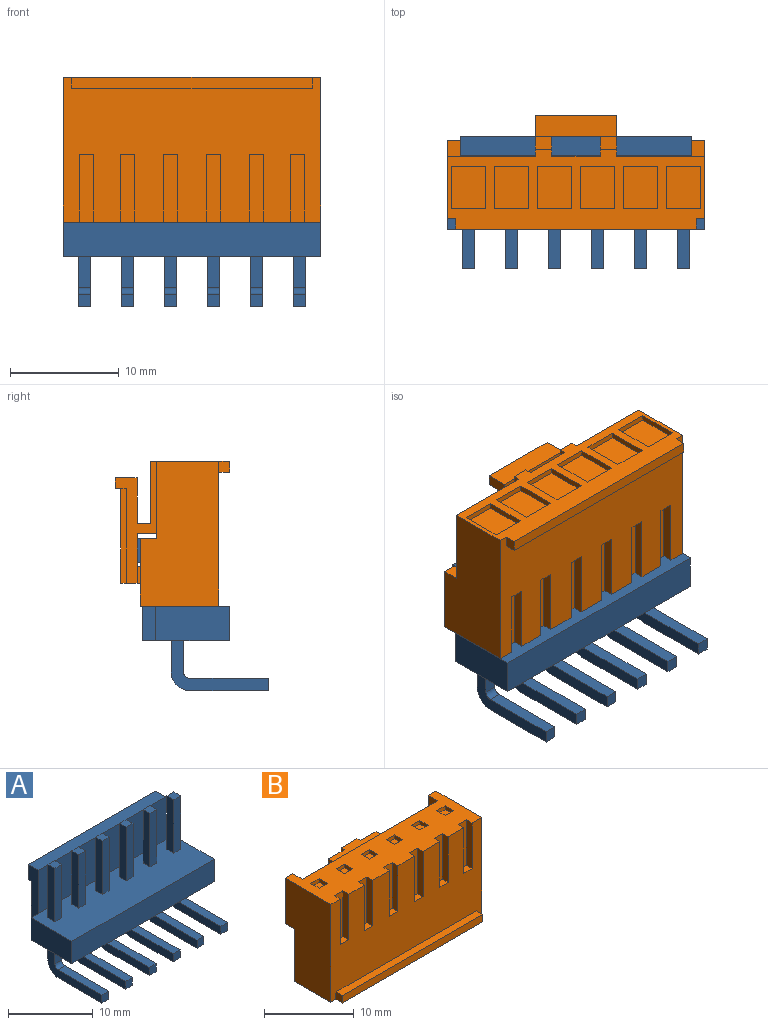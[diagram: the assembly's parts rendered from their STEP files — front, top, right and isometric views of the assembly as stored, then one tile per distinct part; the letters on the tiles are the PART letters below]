
ASSEMBLY  parts=2 mates=1
PART A: 98 faces, bbox 23.7x12.1x15.5 mm
  f0: plane 1.14x1.14mm, normal (0,-1,0), area 1.3mm2, adj f1,f2,f3,f4
  f1: plane 8.97x4.57mm, normal (1,0,0), area 13.6mm2, adj f0,f3,f4,f5,f6,f7,f8,f9
  f2: plane 8.97x4.57mm, normal (-1,0,0), area 13.6mm2, adj f0,f3,f4,f5,f6,f7,f8,f9
  f3: plane 7.26x1.14mm, normal (0,0,1), area 8.3mm2, adj f0,f1,f2,f9
  f4: plane 7.26x1.14mm, normal (0,0,-1), area 8.3mm2, adj f0,f1,f2,f5
  f5: cylinder r=1.71mm len=1.71mm, axis (-1,0,0), area 3.1mm2, adj f1,f2,f4,f6
  f6: plane 2.86x1.14mm, normal (0,1,0), area 3.3mm2, adj f1,f2,f5,f8
  f7: plane 2.86x1.14mm, normal (0,-1,0), area 3.3mm2, adj f1,f2,f8,f9
  f8: plane 23.7x8mm, normal (0,0,-1), area 178.8mm2, adj f1,f2,f6,f7,f10,f11,f12,f13
  f9: cylinder r=0.57mm len=1.14mm, axis (-1,0,0), area 1mm2, adj f1,f2,f3,f7
  f10: plane 3.2x1.25mm, normal (0,1,0), area 4mm2, adj f8,f26,f27,f38
  f11: plane 8.97x4.57mm, normal (1,0,0), area 13.6mm2, adj f8,f24,f35,f39,f40,f41,f42,f43
  f12: plane 9.4x1.7mm, normal (1,0,0), area 12.4mm2, adj f8,f13,f36,f44,f45,f46,f47
  f13: plane 21.2x7.2mm, normal (0,1,0), area 152.6mm2, adj f8,f12,f26,f47
  f14: plane 8.97x4.57mm, normal (-1,0,0), area 13.6mm2, adj f8,f28,f34,f48,f49,f50,f51,f52
  f15: plane 2.86x1.14mm, normal (0,1,0), area 3.3mm2, adj f8,f21,f31,f53
  f16: plane 2.86x1.14mm, normal (0,-1,0), area 3.3mm2, adj f8,f21,f31,f54
  f17: plane 2.86x1.14mm, normal (0,1,0), area 3.3mm2, adj f8,f18,f29,f55
  f18: plane 8.97x4.57mm, normal (1,0,0), area 13.6mm2, adj f8,f17,f37,f55,f56,f57,f58,f59
  f19: plane 8.97x4.57mm, normal (1,0,0), area 13.6mm2, adj f8,f22,f30,f60,f61,f62,f63,f64
  f20: plane 8.97x4.57mm, normal (1,0,0), area 13.6mm2, adj f8,f28,f34,f48,f49,f50,f51,f52
  f21: plane 8.97x4.57mm, normal (1,0,0), area 13.6mm2, adj f8,f15,f16,f53,f54,f65,f66,f67
  f22: plane 2.86x1.14mm, normal (0,1,0), area 3.3mm2, adj f8,f19,f33,f61
  f23: plane 23.7x3.2mm, normal (0,-1,0), area 75.8mm2, adj f8,f27,f32,f38
  f24: plane 2.86x1.14mm, normal (0,1,0), area 3.3mm2, adj f8,f11,f25,f40
  f25: plane 8.97x4.57mm, normal (-1,0,0), area 13.6mm2, adj f8,f24,f35,f39,f40,f41,f42,f43
  f26: plane 9.4x1.7mm, normal (-1,0,0), area 12.4mm2, adj f8,f10,f13,f44,f45,f46,f47
  f27: plane 6.8x3.2mm, normal (-1,0,0), area 21.8mm2, adj f8,f10,f23,f38
  f28: plane 2.86x1.14mm, normal (0,1,0), area 3.3mm2, adj f8,f14,f20,f52
  f29: plane 8.97x4.57mm, normal (-1,0,0), area 13.6mm2, adj f8,f17,f37,f55,f56,f57,f58,f59
  f30: plane 2.86x1.14mm, normal (0,-1,0), area 3.3mm2, adj f8,f19,f33,f62
  f31: plane 8.97x4.57mm, normal (-1,0,0), area 13.6mm2, adj f8,f15,f16,f53,f54,f65,f66,f67
  f32: plane 6.8x3.2mm, normal (1,0,0), area 21.8mm2, adj f8,f23,f36,f38
  f33: plane 8.97x4.57mm, normal (-1,0,0), area 13.6mm2, adj f8,f22,f30,f60,f61,f62,f63,f64
  f34: plane 2.86x1.14mm, normal (0,-1,0), area 3.3mm2, adj f8,f14,f20,f50
  f35: plane 2.86x1.14mm, normal (0,-1,0), area 3.3mm2, adj f8,f11,f25,f39
  f36: plane 3.2x1.25mm, normal (0,1,0), area 4mm2, adj f8,f12,f32,f38
  f37: plane 2.86x1.14mm, normal (0,-1,0), area 3.3mm2, adj f8,f18,f29,f58
  f38: plane 23.7x6.8mm, normal (0,0,1), area 153.4mm2, adj f10,f23,f27,f32,f36,f45,f68,f69
  f39: cylinder r=0.57mm len=1.14mm, axis (-1,0,0), area 1mm2, adj f11,f25,f35,f43
  f40: cylinder r=1.71mm len=1.71mm, axis (-1,0,0), area 3.1mm2, adj f11,f24,f25,f41
  f41: plane 7.26x1.14mm, normal (0,0,-1), area 8.3mm2, adj f11,f25,f40,f42
  f42: plane 1.14x1.14mm, normal (0,-1,0), area 1.3mm2, adj f11,f25,f41,f43
  f43: plane 7.26x1.14mm, normal (0,0,1), area 8.3mm2, adj f11,f25,f39,f42
  f44: plane 21.2x1.7mm, normal (0,0,1), area 36mm2, adj f12,f26,f45,f46
  f45: plane 21.2x6.2mm, normal (0,-1,0), area 131.4mm2, adj f12,f26,f38,f44
  f46: plane 21.2x2.2mm, normal (0,1,0), area 46.6mm2, adj f12,f26,f44,f47
  f47: plane 21.2x0.5mm, normal (0,0,-1), area 10.6mm2, adj f12,f13,f26,f46
  f48: plane 7.26x1.14mm, normal (0,0,-1), area 8.3mm2, adj f14,f20,f49,f52
  f49: plane 1.14x1.14mm, normal (0,-1,0), area 1.3mm2, adj f14,f20,f48,f51
  f50: cylinder r=0.57mm len=1.14mm, axis (-1,0,0), area 1mm2, adj f14,f20,f34,f51
  f51: plane 7.26x1.14mm, normal (0,0,1), area 8.3mm2, adj f14,f20,f49,f50
  f52: cylinder r=1.71mm len=1.71mm, axis (-1,0,0), area 3.1mm2, adj f14,f20,f28,f48
  f53: cylinder r=1.71mm len=1.71mm, axis (-1,0,0), area 3.1mm2, adj f15,f21,f31,f66
  f54: cylinder r=0.57mm len=1.14mm, axis (-1,0,0), area 1mm2, adj f16,f21,f31,f67
  f55: cylinder r=1.71mm len=1.71mm, axis (-1,0,0), area 3.1mm2, adj f17,f18,f29,f57
  f56: plane 1.14x1.14mm, normal (0,-1,0), area 1.3mm2, adj f18,f29,f57,f59
  f57: plane 7.26x1.14mm, normal (0,0,-1), area 8.3mm2, adj f18,f29,f55,f56
  f58: cylinder r=0.57mm len=1.14mm, axis (-1,0,0), area 1mm2, adj f18,f29,f37,f59
  f59: plane 7.26x1.14mm, normal (0,0,1), area 8.3mm2, adj f18,f29,f56,f58
  f60: plane 7.26x1.14mm, normal (0,0,-1), area 8.3mm2, adj f19,f33,f61,f64
  f61: cylinder r=1.71mm len=1.71mm, axis (-1,0,0), area 3.1mm2, adj f19,f22,f33,f60
  f62: cylinder r=0.57mm len=1.14mm, axis (-1,0,0), area 1mm2, adj f19,f30,f33,f63
  f63: plane 7.26x1.14mm, normal (0,0,1), area 8.3mm2, adj f19,f33,f62,f64
  f64: plane 1.14x1.14mm, normal (0,-1,0), area 1.3mm2, adj f19,f33,f60,f63
  f65: plane 1.14x1.14mm, normal (0,-1,0), area 1.3mm2, adj f21,f31,f66,f67
  f66: plane 7.26x1.14mm, normal (0,0,-1), area 8.3mm2, adj f21,f31,f53,f65
  f67: plane 7.26x1.14mm, normal (0,0,1), area 8.3mm2, adj f21,f31,f54,f65
  f68: plane 7.7x1.14mm, normal (0,1,0), area 8.8mm2, adj f38,f74,f80,f92
  f69: plane 7.7x1.14mm, normal (0,-1,0), area 8.8mm2, adj f38,f75,f82,f93
  f70: plane 7.7x1.14mm, normal (0,1,0), area 8.8mm2, adj f38,f76,f84,f94
  f71: plane 7.7x1.14mm, normal (1,0,0), area 8.8mm2, adj f38,f88,f89,f95
  f72: plane 7.7x1.14mm, normal (0,1,0), area 8.8mm2, adj f38,f75,f82,f93
  f73: plane 7.7x1.14mm, normal (-1,0,0), area 8.8mm2, adj f38,f77,f86,f96
  f74: plane 7.7x1.14mm, normal (-1,0,0), area 8.8mm2, adj f38,f68,f90,f92
  f75: plane 7.7x1.14mm, normal (-1,0,0), area 8.8mm2, adj f38,f69,f72,f93
  f76: plane 7.7x1.14mm, normal (-1,0,0), area 8.8mm2, adj f38,f70,f83,f94
  f77: plane 7.7x1.14mm, normal (0,-1,0), area 8.8mm2, adj f38,f73,f78,f96
  f78: plane 7.7x1.14mm, normal (1,0,0), area 8.8mm2, adj f38,f77,f86,f96
  f79: plane 7.7x1.14mm, normal (-1,0,0), area 8.8mm2, adj f38,f88,f89,f95
  f80: plane 7.7x1.14mm, normal (1,0,0), area 8.8mm2, adj f38,f68,f90,f92
  f81: plane 7.7x1.14mm, normal (-1,0,0), area 8.8mm2, adj f38,f87,f91,f97
  f82: plane 7.7x1.14mm, normal (1,0,0), area 8.8mm2, adj f38,f69,f72,f93
  f83: plane 7.7x1.14mm, normal (0,-1,0), area 8.8mm2, adj f38,f76,f84,f94
  f84: plane 7.7x1.14mm, normal (1,0,0), area 8.8mm2, adj f38,f70,f83,f94
  f85: plane 7.7x1.14mm, normal (1,0,0), area 8.8mm2, adj f38,f87,f91,f97
  f86: plane 7.7x1.14mm, normal (0,1,0), area 8.8mm2, adj f38,f73,f78,f96
  f87: plane 7.7x1.14mm, normal (0,1,0), area 8.8mm2, adj f38,f81,f85,f97
  f88: plane 7.7x1.14mm, normal (0,-1,0), area 8.8mm2, adj f38,f71,f79,f95
  f89: plane 7.7x1.14mm, normal (0,1,0), area 8.8mm2, adj f38,f71,f79,f95
  f90: plane 7.7x1.14mm, normal (0,-1,0), area 8.8mm2, adj f38,f74,f80,f92
  f91: plane 7.7x1.14mm, normal (0,-1,0), area 8.8mm2, adj f38,f81,f85,f97
  f92: plane 1.14x1.14mm, normal (0,0,1), area 1.3mm2, adj f68,f74,f80,f90
  f93: plane 1.14x1.14mm, normal (0,0,1), area 1.3mm2, adj f69,f72,f75,f82
  f94: plane 1.14x1.14mm, normal (0,0,1), area 1.3mm2, adj f70,f76,f83,f84
  f95: plane 1.14x1.14mm, normal (0,0,1), area 1.3mm2, adj f71,f79,f88,f89
  f96: plane 1.14x1.14mm, normal (0,0,1), area 1.3mm2, adj f73,f77,f78,f86
  f97: plane 1.14x1.14mm, normal (0,0,1), area 1.3mm2, adj f81,f85,f87,f91
PART B: 124 faces, bbox 23.7x10.5x13.3 mm
  f0: plane 3.9x3.15mm, normal (0,0,-1), area 12.3mm2, adj f1,f2,f3,f4
  f1: plane 3.15x0.5mm, normal (0,1,0), area 1.6mm2, adj f0,f3,f4,f5
  f2: plane 3.15x0.5mm, normal (0,-1,0), area 1.6mm2, adj f0,f3,f4,f5
  f3: plane 3.9x0.5mm, normal (1,0,0), area 1.9mm2, adj f0,f1,f2,f5
  f4: plane 3.9x0.5mm, normal (-1,0,0), area 1.9mm2, adj f0,f1,f2,f5
  f5: plane 23.7x7.3mm, normal (0,0,-1), area 85.3mm2, adj f1,f2,f3,f4,f6,f7,f8,f9
  f6: plane 1x1mm, normal (1,0,0), area 1mm2, adj f5,f10,f36,f39
  f7: plane 6.6x1.8mm, normal (1,0,0), area 5mm2, adj f5,f16,f32,f40,f41,f42
  f8: plane 11.2x3.8mm, normal (-1,0,0), area 15.7mm2, adj f5,f16,f32,f40,f41,f42,f43,f44
  f9: plane 3.15x0.5mm, normal (0,1,0), area 1.6mm2, adj f5,f21,f26,f48
  f10: plane 23.7x13.3mm, normal (0,-1,0), area 244.7mm2, adj f5,f6,f27,f33,f34,f39,f49,f50
  f11: plane 3.15x0.5mm, normal (0,-1,0), area 1.6mm2, adj f5,f23,f28,f68
  f12: plane 3.9x0.5mm, normal (-1,0,0), area 1.9mm2, adj f5,f31,f35,f69
  f13: plane 3.15x0.5mm, normal (0,1,0), area 1.6mm2, adj f5,f23,f28,f68
  f14: plane 3.15x0.5mm, normal (0,-1,0), area 1.6mm2, adj f5,f21,f26,f48
  f15: plane 3.9x0.5mm, normal (-1,0,0), area 1.9mm2, adj f5,f18,f38,f70
  f16: plane 5.7x1.5mm, normal (0,1,0), area 8.5mm2, adj f5,f7,f8,f40
  f17: plane 5.7x1.5mm, normal (0,1,0), area 8.5mm2, adj f5,f20,f22,f71
  f18: plane 3.15x0.5mm, normal (0,-1,0), area 1.6mm2, adj f5,f15,f25,f70
  f19: plane 3.15x0.5mm, normal (0,1,0), area 1.6mm2, adj f5,f29,f30,f72
  f20: plane 11.2x3.8mm, normal (1,0,0), area 15.7mm2, adj f5,f17,f32,f42,f43,f44,f45,f47
  f21: plane 3.9x0.5mm, normal (1,0,0), area 1.9mm2, adj f5,f9,f14,f48
  f22: plane 6.6x1.8mm, normal (-1,0,0), area 5mm2, adj f5,f17,f32,f42,f71,f74
  f23: plane 3.9x0.5mm, normal (1,0,0), area 1.9mm2, adj f5,f11,f13,f68
  f24: plane 3.15x0.5mm, normal (0,-1,0), area 1.6mm2, adj f5,f29,f30,f72
  f25: plane 3.9x0.5mm, normal (1,0,0), area 1.9mm2, adj f5,f18,f38,f70
  f26: plane 3.9x0.5mm, normal (-1,0,0), area 1.9mm2, adj f5,f9,f14,f48
  f27: plane 13.3x7.2mm, normal (-1,0,0), area 85.1mm2, adj f5,f10,f32,f61,f75,f76
  f28: plane 3.9x0.5mm, normal (-1,0,0), area 1.9mm2, adj f5,f11,f13,f68
  f29: plane 3.9x0.5mm, normal (1,0,0), area 1.9mm2, adj f5,f19,f24,f72
  f30: plane 3.9x0.5mm, normal (-1,0,0), area 1.9mm2, adj f5,f19,f24,f72
  f31: plane 3.15x0.5mm, normal (0,1,0), area 1.6mm2, adj f5,f12,f37,f69
  f32: plane 23.7x13.3mm, normal (0,1,0), area 280.5mm2, adj f5,f7,f8,f20,f22,f27,f34,f41
  f33: plane 1x1mm, normal (-1,0,0), area 1mm2, adj f5,f10,f36,f39
  f34: plane 13.3x7.2mm, normal (1,0,0), area 85.1mm2, adj f5,f10,f32,f61,f77,f80
  f35: plane 3.15x0.5mm, normal (0,-1,0), area 1.6mm2, adj f5,f12,f37,f69
  f36: plane 22.1x1mm, normal (0,-1,0), area 22.1mm2, adj f5,f6,f33,f39
  f37: plane 3.9x0.5mm, normal (1,0,0), area 1.9mm2, adj f5,f31,f35,f69
  f38: plane 3.15x0.5mm, normal (0,1,0), area 1.6mm2, adj f5,f15,f25,f70
  f39: plane 22.1x1mm, normal (0,0,1), area 22.1mm2, adj f6,f10,f33,f36
  f40: plane 1.5x1.2mm, normal (0,0,-1), area 1.8mm2, adj f7,f8,f16,f42
  f41: plane 1.8x1.5mm, normal (0,0,1), area 2.7mm2, adj f7,f8,f32,f42
  f42: plane 9.7x7.5mm, normal (0,-1,0), area 63.3mm2, adj f7,f8,f20,f22,f40,f41,f43,f44
  f43: plane 7.5x2.1mm, normal (0,0,1), area 11.5mm2, adj f8,f20,f42,f46,f73,f82,f83,f84
  f44: plane 7.5x2mm, normal (0,0,-1), area 15mm2, adj f8,f20,f42,f47
  f45: plane 7.5x1mm, normal (0,0,1), area 6.3mm2, adj f8,f20,f46,f47,f73,f84,f86,f87
  f46: plane 8.7x2.5mm, normal (0,1,0), area 21.8mm2, adj f8,f43,f45,f87
  f47: plane 7.5x1mm, normal (0,1,0), area 7.5mm2, adj f8,f20,f44,f45
  f48: plane 3.9x3.15mm, normal (0,0,-1), area 12.3mm2, adj f9,f14,f21,f26
  f49: plane 1.3x0.9mm, normal (0,0,1), area 1.2mm2, adj f10,f55,f58,f88
  f50: plane 6.2x0.9mm, normal (1,0,0), area 5.6mm2, adj f10,f52,f61,f89
  f51: plane 6.2x0.9mm, normal (-1,0,0), area 5.6mm2, adj f10,f52,f61,f89
  f52: plane 1.3x0.9mm, normal (0,0,1), area 1.2mm2, adj f10,f50,f51,f89
  f53: plane 6.2x0.9mm, normal (1,0,0), area 5.6mm2, adj f10,f61,f67,f90
  f54: plane 1.3x0.9mm, normal (0,0,1), area 1.2mm2, adj f10,f59,f65,f91
  f55: plane 6.2x0.9mm, normal (1,0,0), area 5.6mm2, adj f10,f49,f61,f88
  f56: plane 1.3x0.9mm, normal (0,0,1), area 1.2mm2, adj f10,f63,f66,f92
  f57: plane 6.2x0.9mm, normal (-1,0,0), area 5.6mm2, adj f10,f61,f67,f90
  f58: plane 6.2x0.9mm, normal (-1,0,0), area 5.6mm2, adj f10,f49,f61,f88
  f59: plane 6.2x0.9mm, normal (-1,0,0), area 5.6mm2, adj f10,f54,f61,f91
  f60: plane 6.2x0.9mm, normal (1,0,0), area 5.6mm2, adj f10,f61,f64,f93
  f61: plane 23.7x7.2mm, normal (0,0,1), area 121.5mm2, adj f10,f27,f32,f34,f50,f51,f53,f55
  f62: plane 6.2x0.9mm, normal (-1,0,0), area 5.6mm2, adj f10,f61,f64,f93
  f63: plane 6.2x0.9mm, normal (-1,0,0), area 5.6mm2, adj f10,f56,f61,f92
  f64: plane 1.3x0.9mm, normal (0,0,1), area 1.2mm2, adj f10,f60,f62,f93
  f65: plane 6.2x0.9mm, normal (1,0,0), area 5.6mm2, adj f10,f54,f61,f91
  f66: plane 6.2x0.9mm, normal (1,0,0), area 5.6mm2, adj f10,f56,f61,f92
  f67: plane 1.3x0.9mm, normal (0,0,1), area 1.2mm2, adj f10,f53,f57,f90
  f68: plane 3.9x3.15mm, normal (0,0,-1), area 12.3mm2, adj f11,f13,f23,f28
  f69: plane 3.9x3.15mm, normal (0,0,-1), area 12.3mm2, adj f12,f31,f35,f37
  f70: plane 3.9x3.15mm, normal (0,0,-1), area 12.3mm2, adj f15,f18,f25,f38
  f71: plane 1.5x1.2mm, normal (0,0,-1), area 1.8mm2, adj f17,f20,f22,f42
  f72: plane 3.9x3.15mm, normal (0,0,-1), area 12.3mm2, adj f19,f24,f29,f30
  f73: plane 8.7x2.5mm, normal (0,1,0), area 21.7mm2, adj f20,f43,f45,f84
  f74: plane 1.8x1.5mm, normal (0,0,1), area 2.7mm2, adj f20,f22,f32,f42
  f75: plane 6.2x1.2mm, normal (0,1,0), area 7.4mm2, adj f27,f61,f76,f78
  f76: plane 1.5x1.2mm, normal (0,0,-1), area 1.8mm2, adj f27,f32,f75,f78
  f77: plane 1.5x1.2mm, normal (0,0,-1), area 1.8mm2, adj f32,f34,f79,f80
  f78: plane 6.2x1.5mm, normal (1,0,0), area 9.3mm2, adj f32,f61,f75,f76
  f79: plane 6.2x1.5mm, normal (-1,0,0), area 9.3mm2, adj f32,f61,f77,f80
  f80: plane 6.2x1.2mm, normal (0,1,0), area 7.4mm2, adj f34,f61,f77,f79
  f81: plane 4.5x0.6mm, normal (0,0,-1), area 2.7mm2, adj f42,f82,f83,f85
  f82: plane 1.5x0.6mm, normal (-1,0,0), area 0.9mm2, adj f42,f43,f81,f85
  f83: plane 1.5x0.6mm, normal (1,0,0), area 0.9mm2, adj f42,f43,f81,f85
  f84: plane 8.7x0.5mm, normal (1,0,0), area 4.3mm2, adj f43,f45,f73,f86
  f85: plane 4.5x1.5mm, normal (0,-1,0), area 6.8mm2, adj f43,f81,f82,f83
  f86: plane 8.7x2.5mm, normal (0,1,0), area 21.8mm2, adj f43,f45,f84,f87
  f87: plane 8.7x0.5mm, normal (-1,0,0), area 4.3mm2, adj f43,f45,f46,f86
  f88: plane 6.2x1.3mm, normal (0,-1,0), area 8.1mm2, adj f49,f55,f58,f61
  f89: plane 6.2x1.3mm, normal (0,-1,0), area 8.1mm2, adj f50,f51,f52,f61
  f90: plane 6.2x1.3mm, normal (0,-1,0), area 8.1mm2, adj f53,f57,f61,f67
  f91: plane 6.2x1.3mm, normal (0,-1,0), area 8.1mm2, adj f54,f59,f61,f65
  f92: plane 6.2x1.3mm, normal (0,-1,0), area 8.1mm2, adj f56,f61,f63,f66
  f93: plane 6.2x1.3mm, normal (0,-1,0), area 8.1mm2, adj f60,f61,f62,f64
  f94: plane 1.3x0.5mm, normal (-1,0,0), area 0.6mm2, adj f61,f109,f113,f118
  f95: plane 1.3x0.5mm, normal (0,-1,0), area 0.6mm2, adj f61,f100,f112,f119
  f96: plane 1.3x0.5mm, normal (-1,0,0), area 0.6mm2, adj f61,f108,f115,f120
  f97: plane 1.3x0.5mm, normal (0,-1,0), area 0.6mm2, adj f61,f101,f104,f121
  f98: plane 1.3x0.5mm, normal (1,0,0), area 0.6mm2, adj f61,f109,f113,f118
  f99: plane 1.3x0.5mm, normal (0,-1,0), area 0.6mm2, adj f61,f102,f105,f122
  f100: plane 1.3x0.5mm, normal (-1,0,0), area 0.6mm2, adj f61,f95,f116,f119
  f101: plane 1.3x0.5mm, normal (-1,0,0), area 0.6mm2, adj f61,f97,f111,f121
  f102: plane 1.3x0.5mm, normal (-1,0,0), area 0.6mm2, adj f61,f99,f117,f122
  f103: plane 1.3x0.5mm, normal (0,1,0), area 0.6mm2, adj f61,f107,f110,f123
  f104: plane 1.3x0.5mm, normal (1,0,0), area 0.6mm2, adj f61,f97,f111,f121
  f105: plane 1.3x0.5mm, normal (1,0,0), area 0.6mm2, adj f61,f99,f117,f122
  f106: plane 1.3x0.5mm, normal (0,-1,0), area 0.6mm2, adj f61,f107,f110,f123
  f107: plane 1.3x0.5mm, normal (-1,0,0), area 0.6mm2, adj f61,f103,f106,f123
  f108: plane 1.3x0.5mm, normal (0,1,0), area 0.6mm2, adj f61,f96,f114,f120
  f109: plane 1.3x0.5mm, normal (0,1,0), area 0.6mm2, adj f61,f94,f98,f118
  f110: plane 1.3x0.5mm, normal (1,0,0), area 0.6mm2, adj f61,f103,f106,f123
  f111: plane 1.3x0.5mm, normal (0,1,0), area 0.6mm2, adj f61,f101,f104,f121
  f112: plane 1.3x0.5mm, normal (1,0,0), area 0.6mm2, adj f61,f95,f116,f119
  f113: plane 1.3x0.5mm, normal (0,-1,0), area 0.6mm2, adj f61,f94,f98,f118
  f114: plane 1.3x0.5mm, normal (1,0,0), area 0.6mm2, adj f61,f108,f115,f120
  f115: plane 1.3x0.5mm, normal (0,-1,0), area 0.6mm2, adj f61,f96,f114,f120
  f116: plane 1.3x0.5mm, normal (0,1,0), area 0.6mm2, adj f61,f100,f112,f119
  f117: plane 1.3x0.5mm, normal (0,1,0), area 0.6mm2, adj f61,f102,f105,f122
  f118: plane 1.3x1.3mm, normal (0,0,1), area 1.7mm2, adj f94,f98,f109,f113
  f119: plane 1.3x1.3mm, normal (0,0,1), area 1.7mm2, adj f95,f100,f112,f116
  f120: plane 1.3x1.3mm, normal (0,0,1), area 1.7mm2, adj f96,f108,f114,f115
  f121: plane 1.3x1.3mm, normal (0,0,1), area 1.7mm2, adj f97,f101,f104,f111
  f122: plane 1.3x1.3mm, normal (0,0,1), area 1.7mm2, adj f99,f102,f105,f117
  f123: plane 1.3x1.3mm, normal (0,0,1), area 1.7mm2, adj f103,f106,f107,f110
PLACE A at identity fixed
PLACE B rot(axis=(0,-1,0),180deg) t=(0,1,5.15)mm
MATE fastened B.f61 <-> A.f38  axis (0,0,-1) through (9.9,4.8,-1.5)mm
